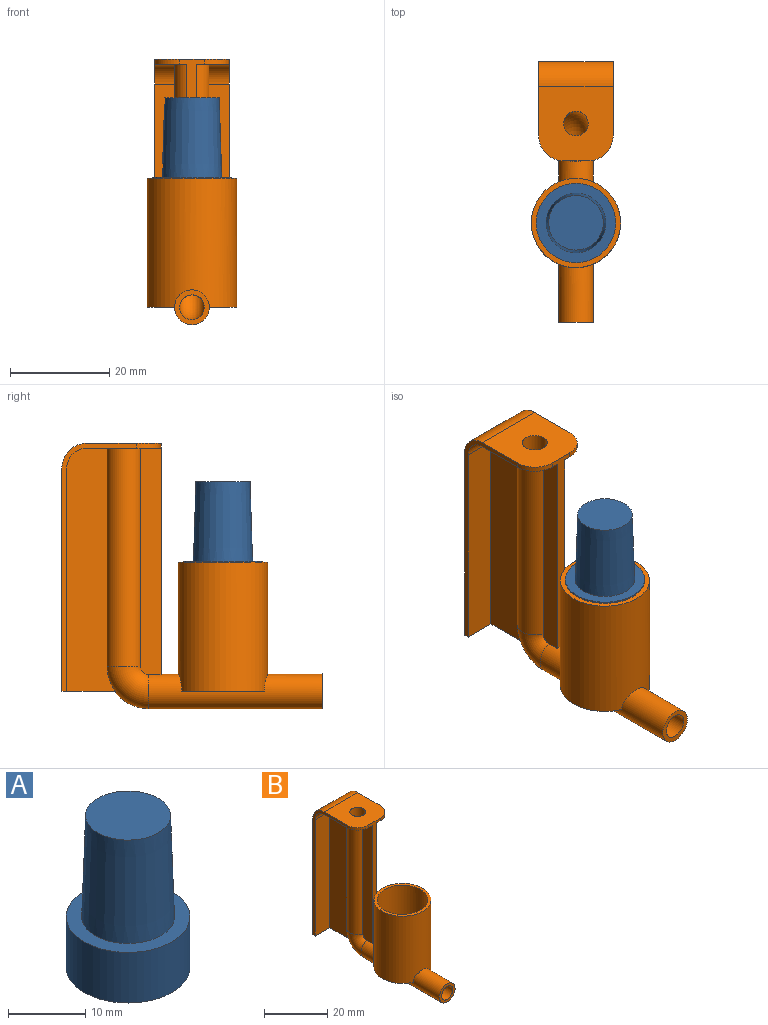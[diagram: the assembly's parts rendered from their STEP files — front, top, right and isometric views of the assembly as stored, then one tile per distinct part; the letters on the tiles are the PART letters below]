
ASSEMBLY  parts=2 mates=1
PART A: 5 faces, bbox 16x16x24 mm
  f0: cylinder r=8mm len=16mm, axis (0,0,-1), area 402.1mm2, adj f1,f2
  f1: plane 16x16mm, normal (0,0,1), area 88mm2, adj f0,f4
  f2: plane 16x16mm, normal (0,0,-1), area 201.1mm2, adj f0
  f3: plane 11x11mm, normal (0,0,1), area 95mm2, adj f4
  f4: cone r=6mm half-angle=1.8deg, axis (0,0,-1), area 578.3mm2, adj f1,f3
PART B: 34 faces, bbox 18x52.5x54.2 mm
  f0: plane 49x9.81mm, normal (-1,0,0), area 398.4mm2, adj f2,f14,f18,f26,f30,f31
  f1: cylinder r=3.5mm len=44mm, axis (0,0,-1), area 394.6mm2, adj f9,f15,f18,f29
  f2: cylinder r=3.5mm len=44mm, axis (0,0,-1), area 394.6mm2, adj f0,f16,f18,f26
  f3: cylinder r=2.5mm len=35mm, axis (0,1,0), area 458.6mm2, adj f17,f19,f21,f22,f23
  f4: plane 16.58x5.5mm, normal (0,0,-1), area 65.9mm2, adj f5,f8
  f5: cylinder r=9mm len=26mm, axis (0,0,-1), area 1431mm2, adj f4,f6,f7,f8
  f6: plane 18x18mm, normal (0,0,1), area 53.4mm2, adj f5,f21
  f7: plane 16.58x5.5mm, normal (0,0,-1), area 65.9mm2, adj f5,f8
  f8: cylinder r=3.5mm len=35mm, axis (0,-1,0), area 574.4mm2, adj f4,f5,f7,f13,f15,f16,f17,f18
  f9: plane 49x9.81mm, normal (1,0,0), area 398.4mm2, adj f1,f14,f18,f29,f32,f33
  f10: plane 45x15mm, normal (0,1,0), area 675mm2, adj f11,f14,f25,f28
  f11: cylinder r=5mm len=15mm, axis (-1,0,0), area 117.8mm2, adj f10,f12,f25,f28
  f12: plane 15x15mm, normal (0,0,1), area 194.6mm2, adj f11,f13,f20,f24,f25,f27,f28
  f13: plane 46.65x5mm, normal (0,-1,0), area 96.1mm2, adj f8,f12,f15,f16,f24,f26,f27,f29
  f14: plane 15x10.81mm, normal (0,0,-1), area 34.4mm2, adj f0,f9,f10,f18,f25,f28,f31,f33
  f15: plane 45.65x4.15mm, normal (1,0,0), area 188.7mm2, adj f1,f8,f13,f18,f29
  f16: plane 45.65x4.15mm, normal (-1,0,0), area 188.7mm2, adj f2,f8,f13,f18,f26
  f17: plane 7x7mm, normal (0,-1,0), area 18.8mm2, adj f3,f8
  f18: torus R=5mm, axis (-1,0,0), area 156.9mm2, adj f0,f1,f2,f8,f9,f14,f15,f16
  f19: torus R=5mm, axis (1,0,0), area 123.4mm2, adj f3,f20
  f20: cylinder r=2.5mm len=45mm, axis (0,0,1), area 706.9mm2, adj f12,f19
  f21: cylinder r=8mm len=25mm, axis (0,0,1), area 1246.6mm2, adj f3,f6,f22,f23
  f22: plane 15.33x5.71mm, normal (0,0,1), area 64.4mm2, adj f3,f21
  f23: plane 15.33x5.71mm, normal (0,0,1), area 64.4mm2, adj f3,f21
  f24: cylinder r=5mm len=5mm, axis (0,0,1), area 7.9mm2, adj f12,f13,f25,f26
  f25: plane 50x15mm, normal (-1,0,0), area 62.1mm2, adj f10,f11,f12,f14,f24,f26,f30,f31
  f26: plane 15x6.5mm, normal (0,0,-1), area 79.8mm2, adj f0,f2,f13,f16,f24,f25,f30
  f27: cylinder r=5mm len=5mm, axis (0,0,1), area 7.9mm2, adj f12,f13,f28,f29
  f28: plane 50x15mm, normal (1,0,0), area 62.1mm2, adj f10,f11,f12,f14,f27,f29,f32,f33
  f29: plane 15x6.5mm, normal (0,0,-1), area 79.8mm2, adj f1,f9,f13,f15,f27,f28,f32
  f30: cylinder r=4mm len=6.5mm, axis (-1,0,0), area 40.8mm2, adj f0,f25,f26,f31
  f31: plane 45x6.5mm, normal (0,-1,0), area 292.5mm2, adj f0,f14,f25,f30
  f32: cylinder r=4mm len=6.5mm, axis (-1,0,0), area 40.8mm2, adj f9,f28,f29,f33
  f33: plane 45x6.5mm, normal (0,-1,0), area 292.5mm2, adj f9,f14,f28,f32
PLACE A t=(-17.38,1.49,5.95)mm
PLACE B t=(-17.38,1.49,-12.32)mm fixed
MATE slider A.f0 <-> B.f5  axis (0,0,-1) through (-17.38,1.49,5.95)mm
